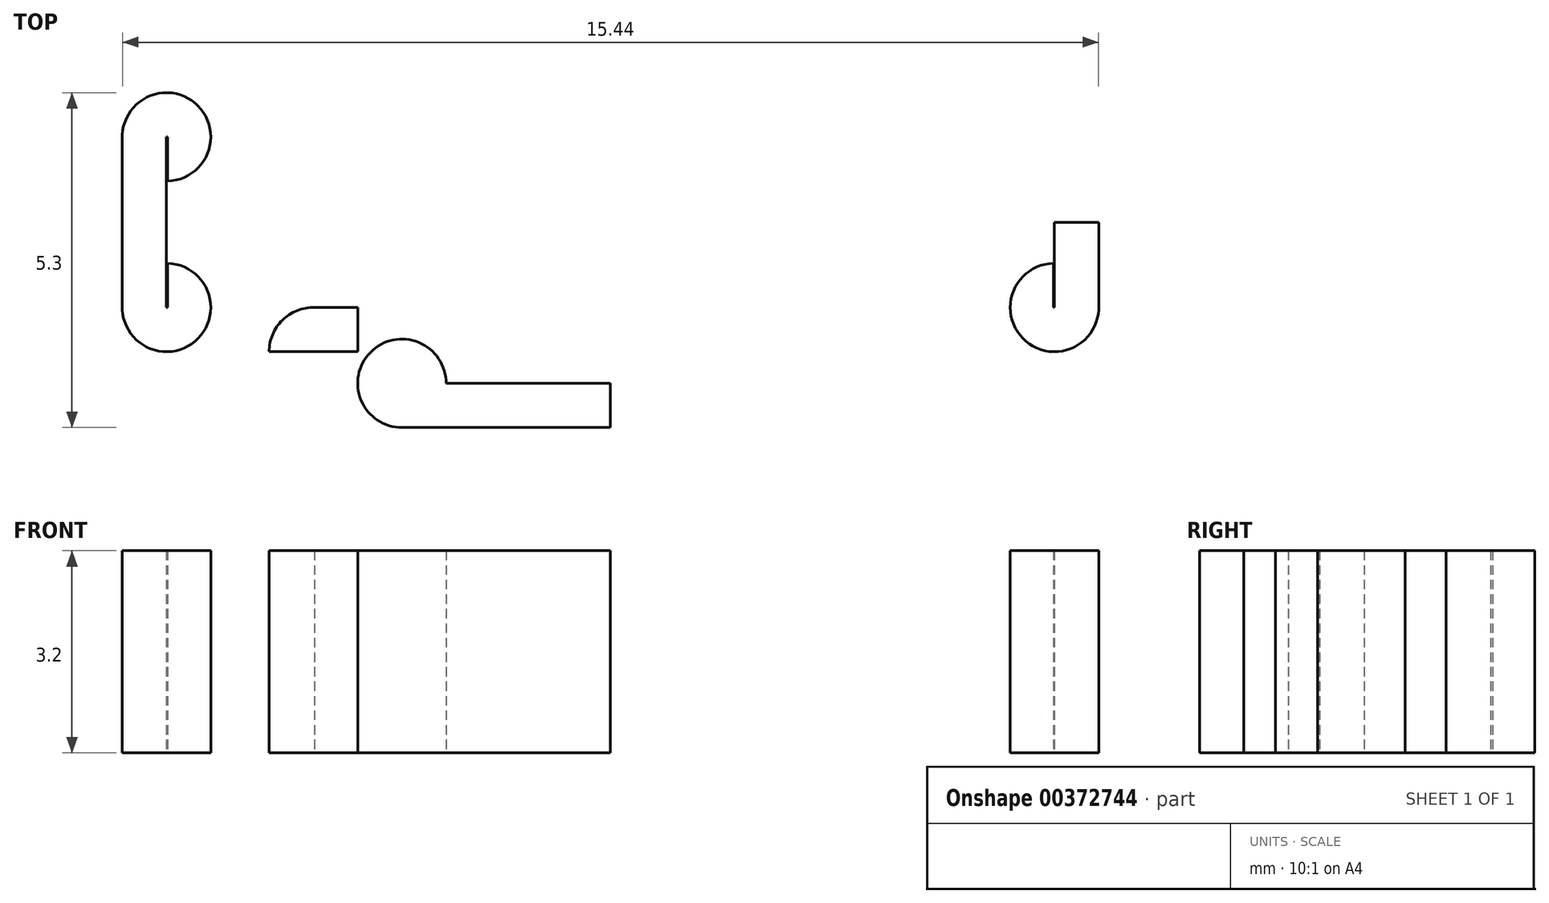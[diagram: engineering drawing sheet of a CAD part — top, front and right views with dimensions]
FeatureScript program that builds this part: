
annotation { "Feature Type Name" : "Feature", "Feature Type Description" : "" }
export const myFeature = defineFeature(function(context is Context, id is Id, definition is map)
    precondition{}
    {
        {
            var Q0;
            Q0=qCreatedBy(makeId("Top.planeOp"),FACE);
            var sketch = newSketch(context, id + "F0", { "sketchPlane" : qUnion([Q0])});
            skLineSegment(sketch, "E0.bottom", {"start": v(0, 0) * mm, "end": v(-4, 0) * mm});
            skLineSegment(sketch, "E0.top", {"start": v(0, 5.3) * mm, "end": v(-4, 5.3) * mm});
            skLineSegment(sketch, "E0.left", {"start": v(0, 0) * mm, "end": v(0, 5.3) * mm});
            skLineSegment(sketch, "E0.right", {"start": v(-4, 0) * mm, "end": v(-4, 5.3) * mm});
            skLineSegment(sketch, "E1.bottom", {"start": v(-4, 4.1) * mm, "end": v(-7.02, 4.1) * mm});
            skLineSegment(sketch, "E1.top", {"start": v(-4, 1.2) * mm, "end": v(-7.02, 1.2) * mm});
            skLineSegment(sketch, "E1.left", {"start": v(-4, 4.1) * mm, "end": v(-4, 1.2) * mm});
            skLineSegment(sketch, "E1.right", {"start": v(-7.02, 4.1) * mm, "end": v(-7.02, 1.2) * mm});
            skCircle(sketch, "E2", {"center": v(-7.02, 4.1) * mm, "radius": 0.7 * mm});
            skCircle(sketch, "E3", {"center": v(-7.02, 1.2) * mm, "radius": 0.7 * mm});
            skLineSegment(sketch, "E4.bottom", {"start": v(-7, 4.8) * mm, "end": v(-4, 4.8) * mm});
            skLineSegment(sketch, "E4.top", {"start": v(-7, 0.5) * mm, "end": v(-4, 0.5) * mm});
            skLineSegment(sketch, "E4.left", {"start": v(-7, 4.8) * mm, "end": v(-7, 0.5) * mm});
            skLineSegment(sketch, "E4.right", {"start": v(-4, 4.8) * mm, "end": v(-4, 0.5) * mm});
            skLineSegment(sketch, "E5", {"start": v(-7.72, 4.07) * mm, "end": v(-7.72, 1.17) * mm});
            skCircle(sketch, "E6", {"center": v(-3.3, 0) * mm, "radius": 0.7 * mm});
            skCircle(sketch, "E7", {"center": v(-4.7, 0.5) * mm, "radius": 0.7 * mm});
            skFitSpline(sketch, "E8", {"points": [v(-5.3, 0.86) * mm, v(-6.56, 0.5) * mm], "startDerivative": vector(-1.02, -1.44) * mm, "endDerivative": vector(-1.95, 0) * mm});
            skPoint(sketch, "E9.0", {"position": v(0, 0) * mm});
            skLineSegment(sketch, "E10.bottom", {"start": v(0, 0) * mm, "end": v(-3.3, 0) * mm});
            skLineSegment(sketch, "E10.top", {"start": v(0, -0.7) * mm, "end": v(-3.3, -0.7) * mm});
            skLineSegment(sketch, "E10.left", {"start": v(0, 0) * mm, "end": v(0, -0.7) * mm});
            skLineSegment(sketch, "E10.right", {"start": v(-3.3, 0) * mm, "end": v(-3.3, -0.7) * mm});
            skFitSpline(sketch, "E11", {"points": [v(-2.85, -0.54) * mm, v(-0.69, 0) * mm], "startDerivative": vector(1.38, 1.04) * mm, "endDerivative": vector(3.53, 0) * mm});
            skLineSegment(sketch, "E12", {"start": v(-7.72, 2.55) * mm, "end": v(0, 2.55) * mm});
            skSolve(sketch);
        }
        {
            var Q0;
            {var subQ0=sQuery(id+"F0.wireOp",EDGE,"E12");var subQ1=sQuery(id+"F0.wireOp",EDGE,"E1.right");var subQ2=makeQuery(id+"F0.imprint","INTERSECT",VERTEX,{"derivedFrom":[subQ1,subQ0]});Q0=makeQuery(id+"F0.imprint","IMPRINT",FACE,{"disambiguationData":[TD([[makeQuery(id+"F0.imprint","IMPRINT",EDGE,{"disambiguationData":[TD([[subQ2,-1.0]])],"derivedFrom":subQ1}),-1.0]])]});}
            var Q1;
            {var subQ3=sQuery(id+"F0.wireOp",EDGE,"E1.right");var subQ8=sQuery(id+"F0.wireOp",EDGE,"E1.top");var subQ9=makeQuery(id+"F0.imprint","INTERSECT",VERTEX,{"derivedFrom":[subQ8,subQ3]});Q1=makeQuery(id+"F0.imprint","IMPRINT",FACE,{"disambiguationData":[TD([[makeQuery(id+"F0.imprint","IMPRINT",EDGE,{"disambiguationData":[TD([[subQ9,1.0]])],"derivedFrom":subQ8}),1.0]])]});}
            var Q2;
            {var subQ0=sQuery(id+"F0.wireOp",EDGE,"E3");var subQ1=sQuery(id+"F0.wireOp",EDGE,"E1.top");var subQ2=makeQuery(id+"F0.imprint","INTERSECT",VERTEX,{"derivedFrom":[subQ1,subQ0]});Q2=makeQuery(id+"F0.imprint","IMPRINT",FACE,{"disambiguationData":[TD([[makeQuery(id+"F0.imprint","IMPRINT",EDGE,{"disambiguationData":[TD([[subQ2,-1.0]])],"derivedFrom":subQ1}),-1.0]])]});}
            var Q3;
            {var subQ0=sQuery(id+"F0.wireOp",EDGE,"E3");var subQ1=sQuery(id+"F0.wireOp",EDGE,"E1.top");var subQ2=makeQuery(id+"F0.imprint","INTERSECT",VERTEX,{"derivedFrom":[subQ1,subQ0]});Q3=makeQuery(id+"F0.imprint","IMPRINT",FACE,{"disambiguationData":[TD([[makeQuery(id+"F0.imprint","IMPRINT",EDGE,{"disambiguationData":[TD([[subQ2,-1.0]])],"derivedFrom":subQ1}),1.0]])]});}
            var Q4;
            {var subQ5=sQuery(id+"F0.wireOp",EDGE,"E1.top");var subQ8=sQuery(id+"F0.wireOp",EDGE,"E7");var subQ10=makeQuery(id+"F0.imprint","INTERSECT",VERTEX,{"disambiguationData":[OD(1.0)],"derivedFrom":[subQ5,subQ8]});Q4=makeQuery(id+"F0.imprint","IMPRINT",FACE,{"disambiguationData":[TD([[makeQuery(id+"F0.imprint","IMPRINT",EDGE,{"disambiguationData":[TD([[subQ10,-1.0]])],"derivedFrom":subQ5}),1.0]])]});}
            var Q5;
            {var subQ5=sQuery(id+"F0.wireOp",EDGE,"E1.top");var subQ7=sQuery(id+"F0.wireOp",EDGE,"E4.right");var subQ11=makeQuery(id+"F0.imprint","INTERSECT",VERTEX,{"derivedFrom":[subQ5,subQ7]});Q5=makeQuery(id+"F0.imprint","IMPRINT",FACE,{"disambiguationData":[TD([[makeQuery(id+"F0.imprint","IMPRINT",EDGE,{"disambiguationData":[TD([[subQ11,-1.0]])],"derivedFrom":subQ5}),-1.0]])]});}
            var Q6;
            {var subQ0=sQuery(id+"F0.wireOp",EDGE,"E4.right");var subQ1=sQuery(id+"F0.wireOp",EDGE,"E1.top");var subQ2=makeQuery(id+"F0.imprint","INTERSECT",VERTEX,{"derivedFrom":[subQ1,subQ0]});Q6=makeQuery(id+"F0.imprint","IMPRINT",FACE,{"disambiguationData":[TD([[makeQuery(id+"F0.imprint","IMPRINT",EDGE,{"disambiguationData":[TD([[subQ2,-1.0]])],"derivedFrom":subQ1}),1.0]])]});}
            var Q7;
            {var subQ0=sQuery(id+"F0.wireOp",EDGE,"E4.right");var subQ1=makeQuery(id+"F0.imprint","INTERSECT",VERTEX,{"derivedFrom":[sQuery(id+"F0.wireOp",EDGE,"E1.top"),subQ0]});Q7=makeQuery(id+"F0.imprint","IMPRINT",FACE,{"disambiguationData":[TD([[makeQuery(id+"F0.imprint","IMPRINT",EDGE,{"disambiguationData":[TD([[subQ1,1.0]])],"derivedFrom":subQ0}),1.0]])]});}
            var Q8;
            {var subQ0=sQuery(id+"F0.wireOp",EDGE,"E10.right");Q8=makeQuery(id+"F0.imprint","IMPRINT",FACE,{"disambiguationData":[TD([[makeQuery(id+"F0.imprint","IMPRINT",EDGE,{"derivedFrom":subQ0}),1.0]])]});}
            var Q9;
            {var subQ1=sQuery(id+"F0.wireOp",EDGE,"E10.top");Q9=makeQuery(id+"F0.imprint","IMPRINT",FACE,{"disambiguationData":[TD([[makeQuery(id+"F0.imprint","IMPRINT",EDGE,{"derivedFrom":subQ1}),-1.0]])]});}
            var Q10;
            {var subQ0=sQuery(id+"F0.wireOp",EDGE,"E0.bottom");Q10=makeQuery(id+"F0.imprint","IMPRINT",FACE,{"disambiguationData":[TD([[makeQuery(id+"F0.imprint","IMPRINT",EDGE,{"derivedFrom":subQ0}),-1.0]])]});}
            var Q11;
            {var subQ0=sQuery(id+"F0.wireOp",EDGE,"E0.bottom");Q11=makeQuery(id+"F0.imprint","IMPRINT",FACE,{"disambiguationData":[TD([[makeQuery(id+"F0.imprint","IMPRINT",EDGE,{"derivedFrom":subQ0}),1.0]])]});}
            var Q12;
            {var subQ0=sQuery(id+"F0.wireOp",EDGE,"E11");Q12=makeQuery(id+"F0.imprint","IMPRINT",FACE,{"disambiguationData":[TD([[makeQuery(id+"F0.imprint","IMPRINT",EDGE,{"derivedFrom":subQ0}),1.0]])]});}
            extrude(context, id + "F1", {"entities" : qUnion([Q0, Q1, Q2, Q3, Q4, Q5, Q6, Q7, Q8, Q9, Q10, Q11, Q12]), "depth" : 3.2 * mm});
        }
        {
            var Q0;
            Q0=makeQuery(id+"F1.opExtrude","SWEPT_BODY",BODY,{"disambiguationData":[OSD([sQuery(id+"F0.wireOp",EDGE,"E0.left"),sQuery(id+"F0.wireOp",EDGE,"E0.right"),sQuery(id+"F0.wireOp",EDGE,"E1.top"),sQuery(id+"F0.wireOp",EDGE,"E1.right"),sQuery(id+"F0.wireOp",EDGE,"E3"),sQuery(id+"F0.wireOp",EDGE,"E4.top"),sQuery(id+"F0.wireOp",EDGE,"E4.left"),sQuery(id+"F0.wireOp",EDGE,"E5"),sQuery(id+"F0.wireOp",EDGE,"E6"),sQuery(id+"F0.wireOp",EDGE,"E7"),sQuery(id+"F0.wireOp",EDGE,"E8"),sQuery(id+"F0.wireOp",EDGE,"E10.top"),sQuery(id+"F0.wireOp",EDGE,"E10.left"),sQuery(id+"F0.wireOp",EDGE,"E12")])]});
            var Q1;
            {var subQ0=sQuery(id+"F0.wireOp",EDGE,"E12");Q1=makeQuery(id+"F1.opExtrude","SWEPT_FACE",FACE,{"disambiguationData":[OSD([subQ0]),TDD([makeQuery(id+"F0.imprint","IMPRINT",EDGE,{"disambiguationData":[TD([[makeQuery(id+"F0.imprint","INTERSECT",VERTEX,{"derivedFrom":[sQuery(id+"F0.wireOp",EDGE,"E4.left"),subQ0]}),-1.0]])],"derivedFrom":subQ0}),makeQuery(id+"F0.imprint","IMPRINT",EDGE,{"disambiguationData":[TD([[makeQuery(id+"F0.imprint","INTERSECT",VERTEX,{"derivedFrom":[sQuery(id+"F0.wireOp",EDGE,"E0.left"),subQ0]}),1.0]])],"derivedFrom":subQ0})])]});}
            mirror(context, id + "F2", {"operationType" : NewBodyOperationType.ADD, "entities" : qUnion([Q0]), "mirrorPlane" : qUnion([Q1])});
        }
        {
            var Q0;
            Q0=makeQuery(id+"F1.opExtrude","SWEPT_BODY",BODY,{"disambiguationData":[OSD([sQuery(id+"F0.wireOp",EDGE,"E0.left"),sQuery(id+"F0.wireOp",EDGE,"E0.right"),sQuery(id+"F0.wireOp",EDGE,"E1.top"),sQuery(id+"F0.wireOp",EDGE,"E1.right"),sQuery(id+"F0.wireOp",EDGE,"E3"),sQuery(id+"F0.wireOp",EDGE,"E4.top"),sQuery(id+"F0.wireOp",EDGE,"E4.left"),sQuery(id+"F0.wireOp",EDGE,"E5"),sQuery(id+"F0.wireOp",EDGE,"E6"),sQuery(id+"F0.wireOp",EDGE,"E7"),sQuery(id+"F0.wireOp",EDGE,"E8"),sQuery(id+"F0.wireOp",EDGE,"E10.top"),sQuery(id+"F0.wireOp",EDGE,"E10.left"),sQuery(id+"F0.wireOp",EDGE,"E12")])]});
            var Q1;
            {var subQ0=makeQuery(id+"F1.opExtrude","SWEPT_FACE",FACE,{"disambiguationData":[OSD([sQuery(id+"F0.wireOp",EDGE,"E0.left"),sQuery(id+"F0.wireOp",EDGE,"E10.left")])]});Q1=makeQuery(id+"F2.boolean.opBoolean","MERGE",FACE,{"derivedFrom":[subQ0,makeQuery(id+"F2.opPattern","COPY",FACE,{"derivedFrom":subQ0,"instanceName":"1"})]});}
            mirror(context, id + "F3", {"operationType" : NewBodyOperationType.ADD, "entities" : qUnion([Q0]), "mirrorPlane" : qUnion([Q1])});
        }
    });
